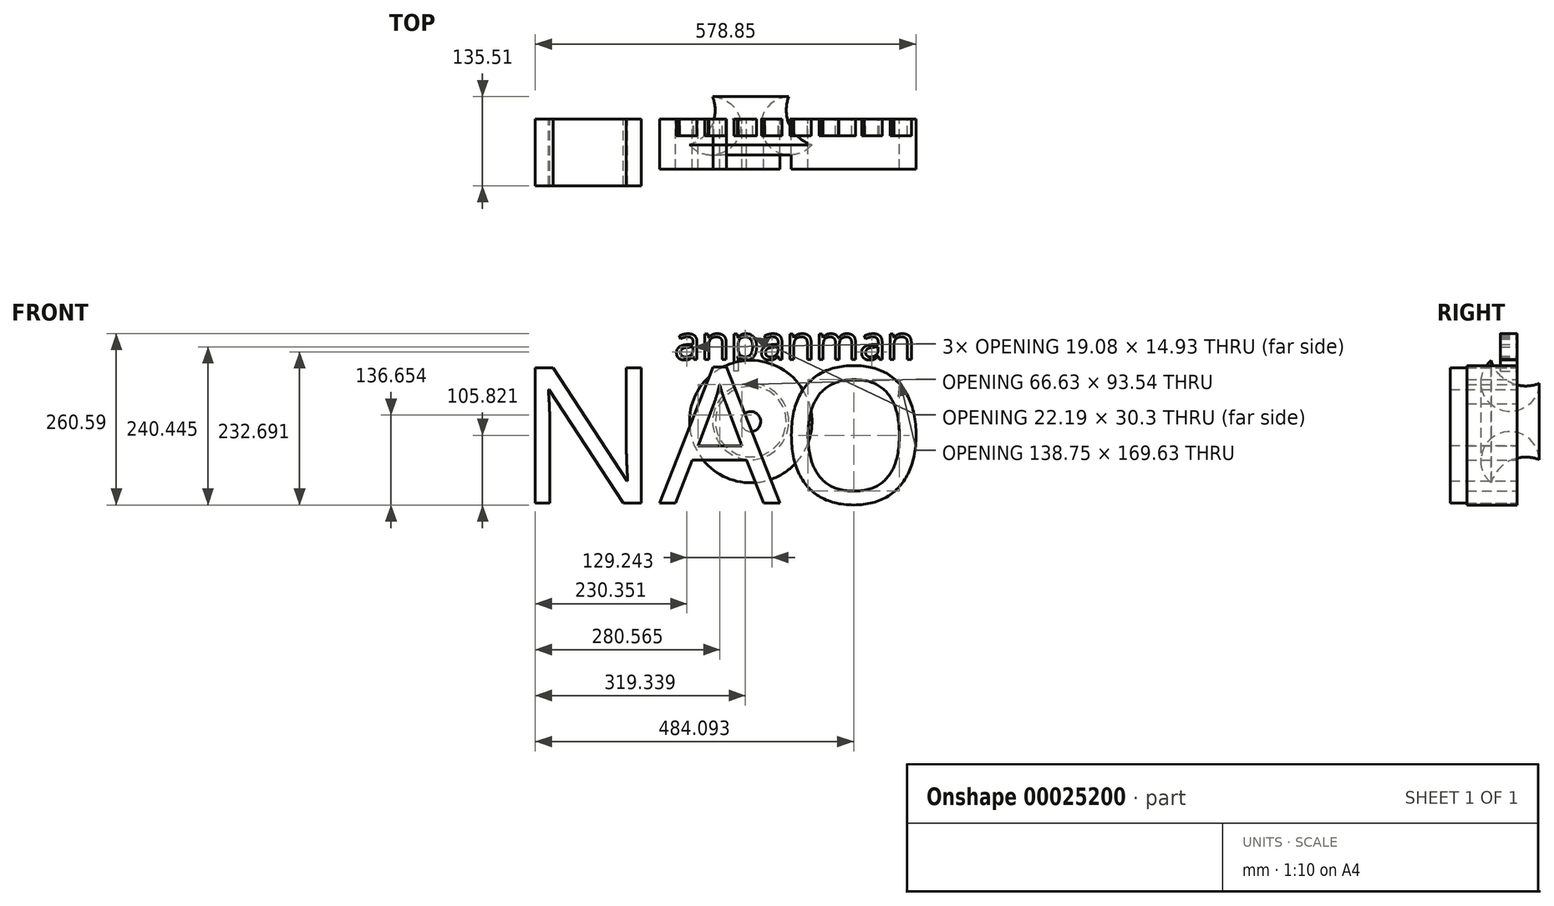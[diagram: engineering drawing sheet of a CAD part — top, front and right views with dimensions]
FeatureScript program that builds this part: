
annotation { "Feature Type Name" : "Feature", "Feature Type Description" : "" }
export const myFeature = defineFeature(function(context is Context, id is Id, definition is map)
    precondition{}
    {
        {
            var Q0;
            Q0=qCreatedBy(makeId("Top.planeOp"),FACE);
            var sketch = newSketch(context, id + "F0", { "sketchPlane" : qUnion([Q0])});
            skCircle(sketch, "E0", {"center": v(65.62, 13.52) * mm, "radius": 55.19 * mm});
            skCircle(sketch, "E1", {"center": v(115.37, -10.36) * mm, "radius": 44.3 * mm});
            skLineSegment(sketch, "E2", {"start": v(174.88, 66.94) * mm, "end": v(174.88, -83.57) * mm});
            skLineSegment(sketch, "E3", {"start": v(172.67, -83.57) * mm, "end": v(174.88, 66.94) * mm});
            skSolve(sketch);
        }
        {
            var Q0;
            {var subQ0=sQuery(id+"F0.wireOp",EDGE,"E1");var subQ1=sQuery(id+"F0.wireOp",EDGE,"E0");var subQ3=makeQuery(id+"F0.imprint","INTERSECT",VERTEX,{"disambiguationData":[OD(0.0)],"derivedFrom":[subQ1,subQ0]});Q0=makeQuery(id+"F0.imprint","IMPRINT",FACE,{"disambiguationData":[TD([[makeQuery(id+"F0.imprint","IMPRINT",EDGE,{"disambiguationData":[TD([[subQ3,-1.0]])],"derivedFrom":subQ1}),-1.0]])]});}
            var Q1;
            Q1=sQuery(id+"F0.wireOp",EDGE,"E2");
            revolve(context, id + "F1", {"entities" : qUnion([Q0]), "axis" : qUnion([Q1]), "revolveType" : RevolveType.FULL});
        }
        {
            var Q0;
            Q0=qCreatedBy(makeId("Front.planeOp"),FACE);
            var sketch = newSketch(context, id + "F2", { "sketchPlane" : qUnion([Q0])});
            skText(sketch, "E4", { "text": "NAO\n", "fontName": "OpenSans-Regular.ttf"});
            const initialGuessF2  = {"E4": [-0.18096, -0.12401, 1, 0, 0.20772]};
            skSetInitialGuess(sketch, initialGuessF2);
            skSolve(sketch);
        }
        {
            var Q0;
            Q0 = qSketchRegion(id + "F2", true);
            extrude(context, id + "F3", {"entities" : qUnion([Q0]), "depth" : 76.2 * mm});
        }
        {
            var Q0;
            Q0=makeQuery(id+"F3.opExtrude","CAP_FACE",FACE,{"disambiguationData":[OSD([sQuery(id+"F2.wireOp",EDGE,"E4.sketch_text.stroke-0"),sQuery(id+"F2.wireOp",EDGE,"E4.sketch_text.stroke-1"),sQuery(id+"F2.wireOp",EDGE,"E4.sketch_text.stroke-2"),sQuery(id+"F2.wireOp",EDGE,"E4.sketch_text.stroke-3"),sQuery(id+"F2.wireOp",EDGE,"E4.sketch_text.stroke-4"),sQuery(id+"F2.wireOp",EDGE,"E4.sketch_text.stroke-5"),sQuery(id+"F2.wireOp",EDGE,"E4.sketch_text.stroke-6"),sQuery(id+"F2.wireOp",EDGE,"E4.sketch_text.stroke-7"),sQuery(id+"F2.wireOp",EDGE,"E4.sketch_text.stroke-8"),sQuery(id+"F2.wireOp",EDGE,"E4.sketch_text.stroke-9"),sQuery(id+"F2.wireOp",EDGE,"E4.sketch_text.stroke-10"),sQuery(id+"F2.wireOp",EDGE,"E4.sketch_text.stroke-11"),sQuery(id+"F2.wireOp",EDGE,"E4.sketch_text.stroke-12"),sQuery(id+"F2.wireOp",EDGE,"E4.sketch_text.stroke-13"),sQuery(id+"F2.wireOp",EDGE,"E4.sketch_text.stroke-14")])],"isStart":false});
            extrude(context, id + "F4", {"entities" : qUnion([Q0]), "operationType" : NewBodyOperationType.ADD, "depth" : 25.4 * mm});
        }
        {
            var Q0;
            Q0=qCreatedBy(makeId("Front.planeOp"),FACE);
            var sketch = newSketch(context, id + "F5", { "sketchPlane" : qUnion([Q0])});
            skText(sketch, "E5", { "text": "anpanman\n", "fontName": "OpenSans-Regular.ttf"});
            const initialGuessF5  = {"E5": [0.05867, 0.09423, 1, 0, 0.0522]};
            skSetInitialGuess(sketch, initialGuessF5);
            skSolve(sketch);
        }
        {
            var Q0;
            Q0 = qSketchRegion(id + "F5", true);
            extrude(context, id + "F6", {"entities" : qUnion([Q0]), "depth" : 25.4 * mm});
        }
    });
